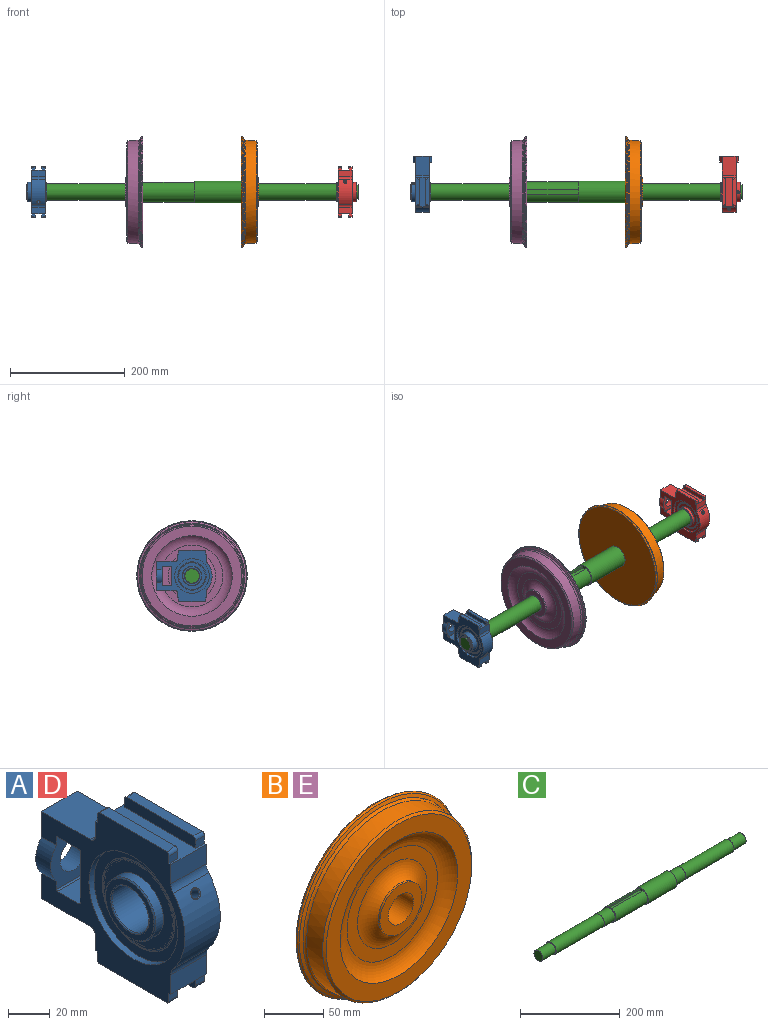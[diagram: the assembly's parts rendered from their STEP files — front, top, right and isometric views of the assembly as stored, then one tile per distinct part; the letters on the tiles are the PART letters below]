
ASSEMBLY  parts=5 mates=5
PART A: 115 faces, bbox 35.7x97x89 mm
  f0: sphere r=26mm, area 36.4mm2, adj f56,f93
  f1: sphere r=26mm, area 36.4mm2, adj f57,f92
  f2: cylinder r=35mm len=44.2mm, axis (-1,0,0), area 1121mm2, adj f3,f4,f22,f23,f53
  f3: plane 97x88.61mm, normal (1,0,0), area 3115.7mm2, adj f2,f5,f11,f13,f17,f19,f21,f22
  f4: plane 97x88.61mm, normal (-1,0,0), area 3115.7mm2, adj f2,f7,f9,f10,f12,f14,f15,f16
  f5: plane 46.12x6mm, normal (0.03,0,1), area 273.4mm2, adj f3,f6,f17,f19
  f6: plane 48.45x6.5mm, normal (-1,0,0), area 313.1mm2, adj f5,f17,f19,f35,f36,f37
  f7: plane 46.12x6mm, normal (-0.03,0,1), area 273.4mm2, adj f4,f8,f16,f18
  f8: plane 48.45x6.5mm, normal (1,0,0), area 313.1mm2, adj f7,f15,f16,f18,f20,f35
  f9: plane 6x4.46mm, normal (0,-1,0), area 26.8mm2, adj f4,f10,f25,f39
  f10: cylinder r=2.04mm len=6mm, axis (-1,0,0), area 15.6mm2, adj f4,f9,f39,f41
  f11: cylinder r=2.04mm len=6mm, axis (-1,0,0), area 15.6mm2, adj f3,f26,f38,f40
  f12: cylinder r=2.04mm len=6mm, axis (-1,0,0), area 15.6mm2, adj f4,f14,f39,f41
  f13: cylinder r=2.04mm len=6mm, axis (-1,0,0), area 15.6mm2, adj f3,f27,f38,f40
  f14: plane 6x4.46mm, normal (0,1,0), area 26.8mm2, adj f4,f12,f25,f39
  f15: plane 6x4.46mm, normal (0,1,0), area 26.8mm2, adj f4,f8,f16,f35
  f16: cylinder r=2.04mm len=6mm, axis (-1,0,0), area 15.6mm2, adj f4,f7,f8,f15
  f17: cylinder r=2.04mm len=6mm, axis (-1,0,0), area 15.6mm2, adj f3,f5,f6,f36
  f18: cylinder r=2.04mm len=6mm, axis (-1,0,0), area 15.6mm2, adj f4,f7,f8,f20
  f19: cylinder r=2.04mm len=6mm, axis (-1,0,0), area 15.6mm2, adj f3,f5,f6,f37
  f20: plane 6x4.46mm, normal (0,-1,0), area 26.8mm2, adj f4,f8,f18,f35
  f21: plane 24x11.29mm, normal (0,-1,0), area 270.9mm2, adj f3,f4,f22,f35
  f22: cylinder r=7.3mm len=24mm, axis (-1,0,0), area 119.7mm2, adj f2,f3,f4,f21
  f23: cylinder r=7.3mm len=24mm, axis (-1,0,0), area 119.7mm2, adj f2,f3,f4,f24
  f24: plane 24x11.29mm, normal (0,-1,0), area 270.9mm2, adj f3,f4,f23,f25
  f25: plane 51x24mm, normal (0,0,-1), area 642.6mm2, adj f3,f4,f9,f14,f24,f26,f27,f28
  f26: plane 6x4.46mm, normal (0,-1,0), area 26.8mm2, adj f3,f11,f25,f38
  f27: plane 6x4.46mm, normal (0,1,0), area 26.8mm2, adj f3,f13,f25,f38
  f28: plane 24x8.85mm, normal (0,1,0), area 212.4mm2, adj f3,f4,f25,f29
  f29: cylinder r=3.65mm len=24mm, axis (-1,0,0), area 137.6mm2, adj f3,f4,f28,f30
  f30: plane 32.85x24mm, normal (0,0,-1), area 788.4mm2, adj f3,f4,f29,f31
  f31: plane 51x32mm, normal (0,1,0), area 1056.5mm2, adj f3,f4,f30,f32,f50,f51,f52
  f32: plane 32.85x24mm, normal (0,0,1), area 788.4mm2, adj f3,f4,f31,f33
  f33: cylinder r=3.65mm len=24mm, axis (-1,0,0), area 137.6mm2, adj f3,f4,f32,f34
  f34: plane 24x8.85mm, normal (0,1,0), area 212.4mm2, adj f3,f4,f33,f35
  f35: plane 51x24mm, normal (0,0,1), area 642.6mm2, adj f3,f4,f6,f8,f15,f20,f21,f34
  f36: plane 6x4.46mm, normal (0,1,0), area 26.8mm2, adj f3,f6,f17,f35
  f37: plane 6x4.46mm, normal (0,-1,0), area 26.8mm2, adj f3,f6,f19,f35
  f38: plane 48.45x6.5mm, normal (-1,0,0), area 313.1mm2, adj f11,f13,f25,f26,f27,f40
  f39: plane 48.45x6.5mm, normal (1,0,0), area 313.1mm2, adj f9,f10,f12,f14,f25,f41
  f40: plane 46.12x6mm, normal (0.03,0,-1), area 273.4mm2, adj f3,f11,f13,f38
  f41: plane 46.12x6mm, normal (-0.03,0,-1), area 273.4mm2, adj f4,f10,f12,f39
  f42: plane 24x14.4mm, normal (0,0,1), area 345.6mm2, adj f3,f4,f48,f49
  f43: plane 30.4x24mm, normal (0,1,0), area 729.6mm2, adj f3,f4,f47,f49
  f44: plane 32x30.4mm, normal (0,-1,0), area 562.1mm2, adj f3,f4,f46,f48,f50,f51,f52
  f45: plane 24x14.4mm, normal (0,0,-1), area 345.6mm2, adj f3,f4,f46,f47
  f46: cylinder r=0.8mm len=24mm, axis (-1,0,0), area 30.2mm2, adj f3,f4,f44,f45
  f47: cylinder r=0.8mm len=24mm, axis (1,0,0), area 30.2mm2, adj f3,f4,f43,f45
  f48: cylinder r=0.8mm len=24mm, axis (1,0,0), area 30.2mm2, adj f3,f4,f42,f44
  f49: cylinder r=0.8mm len=24mm, axis (-1,0,0), area 30.2mm2, adj f3,f4,f42,f43
  f50: cylinder r=16mm len=21.17mm, axis (0,-1,0), area 231.3mm2, adj f4,f31,f44
  f51: cylinder r=16mm len=21.17mm, axis (0,-1,0), area 231.3mm2, adj f3,f31,f44
  f52: cylinder r=9.5mm len=19mm, axis (0,-1,0), area 596.9mm2, adj f31,f44
  f53: cone r=2.46mm half-angle=45deg, axis (0,-0.87,0.5), area 11.5mm2, adj f2,f54
  f54: cylinder r=2.46mm len=9.89mm, axis (0,-0.87,0.5), area 132.5mm2, adj f53,f98
  f55: cylinder r=30mm len=60mm, axis (1,0,0), area 659.7mm2, adj f4,f56
  f56: plane 60x60mm, normal (-1,0,0), area 930.7mm2, adj f0,f55
  f57: plane 60x60mm, normal (1,0,0), area 930.7mm2, adj f1,f58
  f58: cylinder r=30mm len=60mm, axis (-1,0,0), area 659.7mm2, adj f3,f57
  f59: plane 4.92x4.26mm, normal (0,-0.87,0.5), area 19mm2, adj f60
  f60: cone r=2.46mm half-angle=45deg, axis (0,0.87,-0.5), area 13.1mm2, adj f59,f82
  f61: plane 4.92x4.26mm, normal (0,0.87,-0.5), area 11.2mm2, adj f62,f63,f64,f65,f66,f67,f68
  f62: cone r=3mm half-angle=45deg, axis (0,-0.87,0.5), area 13.1mm2, adj f61,f81
  f63: plane 1.73x0.97mm, normal (0,-0.5,-0.87), area 1.9mm2, adj f61,f64,f68,f69
  f64: plane 1.86x1.72mm, normal (-0.87,-0.25,-0.43), area 1.9mm2, adj f61,f63,f65,f69
  f65: plane 1.86x1.72mm, normal (-0.87,0.25,0.43), area 1.9mm2, adj f61,f64,f66,f69
  f66: plane 1.73x0.97mm, normal (0,0.5,0.87), area 1.9mm2, adj f61,f65,f67,f69
  f67: plane 1.86x1.72mm, normal (0.87,0.25,0.43), area 1.9mm2, adj f61,f66,f68,f69
  f68: plane 1.86x1.72mm, normal (0.87,-0.25,-0.43), area 1.9mm2, adj f61,f63,f67,f69
  f69: plane 3.46x2.6mm, normal (0,0.87,-0.5), area 7.8mm2, adj f63,f64,f65,f66,f67,f68
  f70: plane 4.92x4.92mm, normal (0,0,-1), area 19mm2, adj f71
  f71: cone r=2.46mm half-angle=45deg, axis (0,0,1), area 13.1mm2, adj f70,f84
  f72: plane 4.92x4.92mm, normal (0,0,1), area 11.2mm2, adj f73,f74,f75,f76,f77,f78,f79
  f73: cone r=3mm half-angle=45deg, axis (0,0,-1), area 13.1mm2, adj f72,f83
  f74: plane 1.73x1.13mm, normal (0,1,0), area 1.9mm2, adj f72,f75,f79,f80
  f75: plane 1.5x1.13mm, normal (-0.87,0.5,0), area 1.9mm2, adj f72,f74,f76,f80
  f76: plane 1.5x1.13mm, normal (-0.87,-0.5,0), area 1.9mm2, adj f72,f75,f77,f80
  f77: plane 1.73x1.13mm, normal (0,-1,0), area 1.9mm2, adj f72,f76,f78,f80
  f78: plane 1.5x1.13mm, normal (0.87,-0.5,0), area 1.9mm2, adj f72,f77,f79,f80
  f79: plane 1.5x1.13mm, normal (0.87,0.5,0), area 1.9mm2, adj f72,f74,f78,f80
  f80: plane 3.46x3mm, normal (0,0,1), area 7.8mm2, adj f74,f75,f76,f77,f78,f79
  f81: cone r=3mm half-angle=45deg, axis (0,0.87,-0.5), area 10.8mm2, adj f62,f96
  f82: cylinder r=3mm len=6mm, axis (0,0.87,-0.5), area 13.6mm2, adj f60,f91
  f83: cone r=3mm half-angle=45deg, axis (0,0,1), area 10.8mm2, adj f73,f96
  f84: cylinder r=3mm len=6mm, axis (0,0,1), area 13.6mm2, adj f71,f91
  f85: plane 32.8x32.8mm, normal (-1,0,0), area 305.8mm2, adj f86,f90
  f86: cone r=16.4mm half-angle=45deg, axis (1,0,0), area 89mm2, adj f85,f97
  f87: cone r=17mm half-angle=45deg, axis (-1,0,0), area 89mm2, adj f88,f96
  f88: plane 32.8x32.8mm, normal (1,0,0), area 305.8mm2, adj f87,f89
  f89: torus R=13.1mm, axis (-1,0,0), area 75.3mm2, adj f88,f91
  f90: torus R=13.1mm, axis (-1,0,0), area 75.3mm2, adj f85,f91
  f91: cylinder r=12.5mm len=32.8mm, axis (-1,0,0), area 2519mm2, adj f82,f84,f89,f90
  f92: torus R=23.81mm, axis (-1,0,0), area 133.9mm2, adj f1,f95
  f93: torus R=23.81mm, axis (1,0,0), area 133.9mm2, adj f0,f94
  f94: plane 47.61x47.61mm, normal (-1,0,0), area 872.5mm2, adj f93,f97
  f95: plane 47.61x47.61mm, normal (1,0,0), area 872.5mm2, adj f92,f96
  f96: cylinder r=17mm len=34mm, axis (-1,0,0), area 1060mm2, adj f81,f83,f87,f95
  f97: cylinder r=17mm len=34mm, axis (-1,0,0), area 555.4mm2, adj f86,f94
  f98: sphere r=26mm, area 19mm2, adj f54
  f99: cylinder r=17mm len=34mm, axis (-1,0,0), area 560.2mm2, adj f100,f101
  f100: torus R=20.01mm, axis (1,0,0), area 839.1mm2, adj f99,f103
  f101: plane 46.02x46.02mm, normal (1,0,0), area 755.5mm2, adj f99,f103
  f102: cylinder r=0.42mm len=2.7mm, axis (0,0,1), area 7mm2, adj f103,f106
  f103: cylinder r=23.01mm len=46.02mm, axis (1,0,0), area 757.1mm2, adj f100,f101,f102,f104
  f104: cylinder r=0.42mm len=2.83mm, axis (0,0.97,-0.26), area 7mm2, adj f103,f105
  f105: sphere r=26mm, area 0.6mm2, adj f104
  f106: sphere r=26mm, area 0.6mm2, adj f102
  f107: cylinder r=17mm len=34mm, axis (-1,0,0), area 560.2mm2, adj f108,f109
  f108: torus R=20.01mm, axis (1,0,0), area 839.1mm2, adj f107,f111
  f109: plane 46.02x46.02mm, normal (-1,0,0), area 755.5mm2, adj f107,f111
  f110: cylinder r=0.42mm len=2.76mm, axis (0,0.87,-0.5), area 7mm2, adj f111,f114
  f111: cylinder r=23.01mm len=46.02mm, axis (1,0,0), area 757.1mm2, adj f108,f109,f110,f112
  f112: cylinder r=0.42mm len=2.76mm, axis (0,-0.5,-0.87), area 7mm2, adj f111,f113
  f113: sphere r=26mm, area 0.6mm2, adj f112
  f114: sphere r=26mm, area 0.6mm2, adj f110
PART B: 14 faces, bbox 207.9x39.8x207.9 mm
  f0: plane 107.8x107.8mm, normal (0,-1,0), area 3743.8mm2, adj f4,f5
  f1: plane 187.88x187.88mm, normal (0,1,0), area 27016.8mm2, adj f9,f13
  f2: cone r=90mm half-angle=3deg, axis (0,1,0), area 10154.5mm2, adj f6,f7
  f3: plane 173.36x173.36mm, normal (0,-1,0), area 8208.9mm2, adj f5,f7
  f4: torus R=41.4mm, axis (0,-1,0), area 3909.1mm2, adj f0,f11
  f5: torus R=53.9mm, axis (0,1,0), area 7325.1mm2, adj f0,f3
  f6: torus R=93.02mm, axis (0,-1,0), area 1828.6mm2, adj f2,f8
  f7: cone r=86.68mm half-angle=48deg, axis (0,1,0), area 1646.4mm2, adj f2,f3
  f8: cone r=91.48mm half-angle=68.9deg, axis (0,1,0), area 2025.2mm2, adj f6,f10
  f9: torus R=93.94mm, axis (0,-1,0), area 1936.6mm2, adj f1,f10
  f10: torus R=93.96mm, axis (0,1,0), area 1304.7mm2, adj f8,f9
  f11: cylinder r=25mm len=50mm, axis (0,1,0), area 314.2mm2, adj f4,f12
  f12: plane 50x50mm, normal (0,-1,0), area 1256.6mm2, adj f11,f13
  f13: cylinder r=15mm len=30mm, axis (0,-1,0), area 2827.4mm2, adj f1,f12
PART C: 21 faces, bbox 577.4x38.1x38.1 mm
  f0: plane 29x29mm, normal (1,0,0), area 169.6mm2, adj f18,f19
  f1: plane 30x30mm, normal (1,0,0), area 46.3mm2, adj f17,f18
  f2: plane 38.1x38.1mm, normal (1,0,0), area 433.2mm2, adj f16,f17
  f3: cylinder r=12.5mm len=36mm, axis (-1,0,0), area 2827.4mm2, adj f4,f5
  f4: plane 25x25mm, normal (-1,0,0), area 490.9mm2, adj f3
  f5: plane 29x29mm, normal (-1,0,0), area 169.6mm2, adj f3,f6
  f6: cylinder r=14.5mm len=136.95mm, axis (-1,0,0), area 12477mm2, adj f5,f7
  f7: plane 30x30mm, normal (-1,0,0), area 46.3mm2, adj f6,f8
  f8: cylinder r=15mm len=30mm, axis (-1,0,0), area 2827.4mm2, adj f7,f9,f11
  f9: plane 35x34.27mm, normal (-1,0,0), area 229.8mm2, adj f8,f10,f12,f14
  f10: cylinder r=17.5mm len=90mm, axis (-1,0,0), area 8983.3mm2, adj f9,f12,f14,f15
  f11: plane 10x2.5mm, normal (1,0,0), area 22.2mm2, adj f8,f12,f13,f14
  f12: plane 90x4.27mm, normal (0,-1,0), area 384.3mm2, adj f9,f10,f11,f13,f15
  f13: plane 90x10mm, normal (0,0,1), area 900mm2, adj f11,f12,f14,f15
  f14: plane 90x4.27mm, normal (0,1,0), area 384.3mm2, adj f9,f10,f11,f13,f15
  f15: plane 38.1x38.1mm, normal (-1,0,0), area 225.6mm2, adj f10,f12,f13,f14,f16
  f16: cylinder r=19.05mm len=81.5mm, axis (-1,0,0), area 9755.1mm2, adj f2,f15
  f17: cylinder r=15mm len=30mm, axis (-1,0,0), area 2827.4mm2, adj f1,f2
  f18: cylinder r=14.5mm len=136.95mm, axis (-1,0,0), area 12477mm2, adj f0,f1
  f19: cylinder r=12.5mm len=36mm, axis (-1,0,0), area 2827.4mm2, adj f0,f20
  f20: plane 25x25mm, normal (1,0,0), area 490.9mm2, adj f19
PART D: same geometry as A
PART E: same geometry as B
PLACE A rot(axis=(0,1,0),180deg) t=(21.7,0,0)mm
PLACE B rot(axis=(0.58,-0.58,0.58),120deg) t=(374.45,0,0)mm
PLACE C at identity fixed
PLACE D t=(555.1,0,0)mm
PLACE E rot(axis=(-0.58,-0.58,-0.58),120deg) t=(202.95,0,0)mm
MATE fastened B.f2 <-> C.f3  axis (1,0,0) through (404.45,0,0)mm
MATE revolute C.f3 <-> A.f86  axis (-1,0,0) through (36,0,0)mm
MATE revolute C.f3 <-> D.f86  axis (-1,0,0) through (541.4,0,0)mm
MATE fastened E.f2 <-> C.f3  axis (-1,0,0) through (172.95,0,0)mm
MATE parallel D.f35 <-> A.f25  axis (0,0,1) through (555.1,0,38)mm
